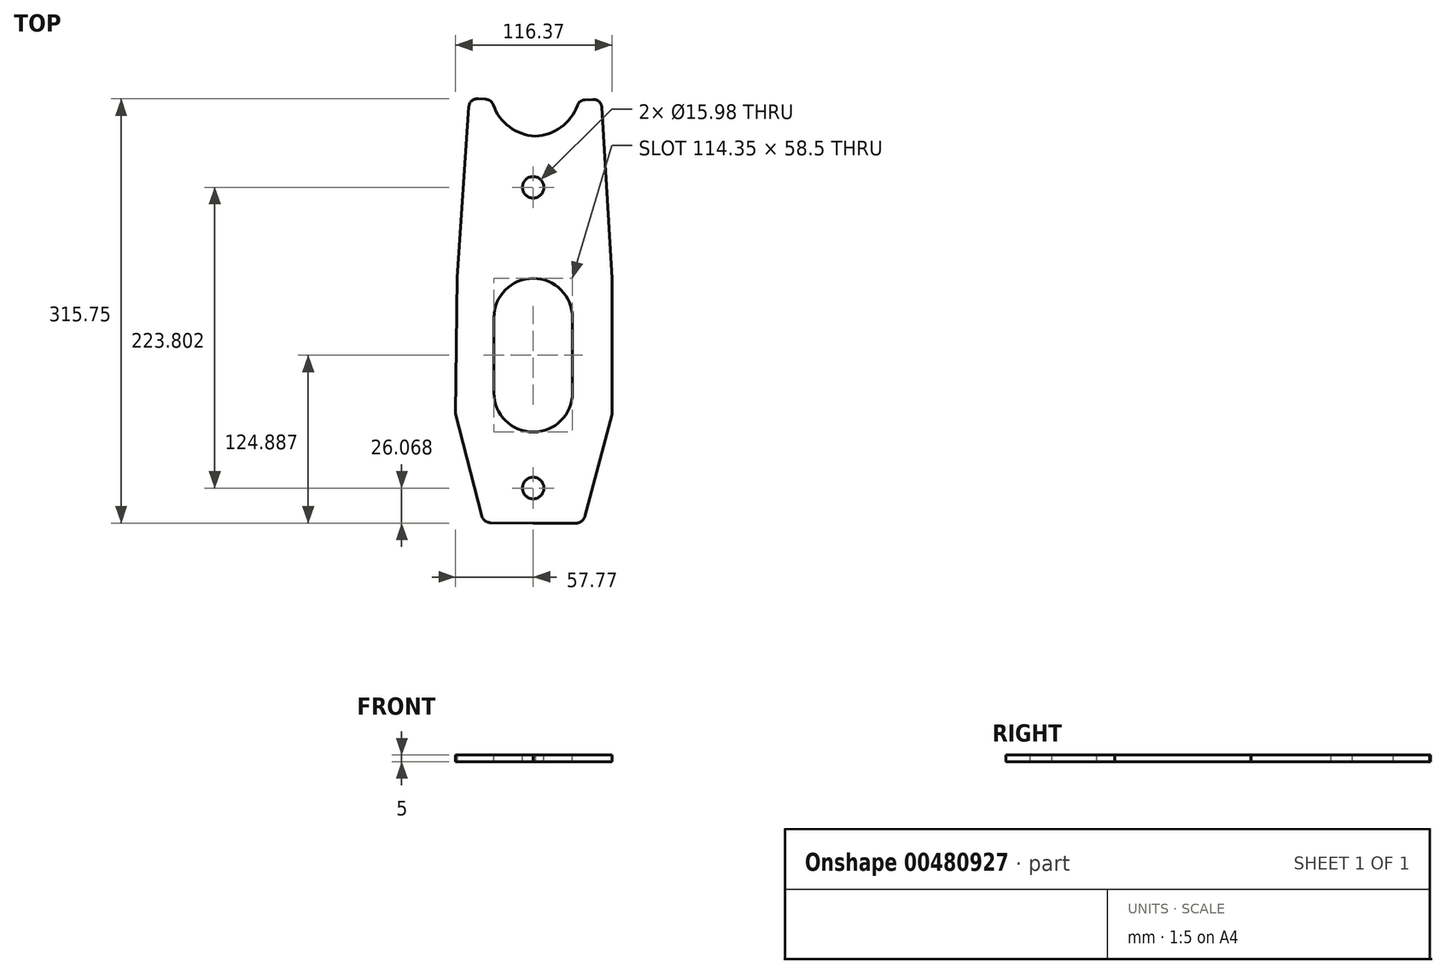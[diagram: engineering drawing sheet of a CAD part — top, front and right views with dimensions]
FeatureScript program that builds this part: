
annotation { "Feature Type Name" : "Feature", "Feature Type Description" : "" }
export const myFeature = defineFeature(function(context is Context, id is Id, definition is map)
    precondition{}
    {
        {
            var Q0;
            Q0=qCreatedBy(makeId("Top.planeOp"),FACE);
            var sketch = newSketch(context, id + "F0", { "sketchPlane" : qUnion([Q0])});
            skLineSegment(sketch, "E0", {"start": v(0, 0) * mm, "end": v(36.98, 0) * mm});
            skLineSegment(sketch, "E1", {"start": v(36.98, 0) * mm, "end": v(58.6, 0) * mm, "construction": true});
            skLineSegment(sketch, "E2", {"start": v(58.6, 0) * mm, "end": v(58.6, 80.74) * mm, "construction": true});
            skLineSegment(sketch, "E3", {"start": v(58.6, 80.74) * mm, "end": v(36.98, 0) * mm});
            skLineSegment(sketch, "E4", {"start": v(58.6, 80.74) * mm, "end": v(58.6, 182.06) * mm});
            skLineSegment(sketch, "E5", {"start": v(58.6, 182.06) * mm, "end": v(58.6, 315.68) * mm, "construction": true});
            skLineSegment(sketch, "E6", {"start": v(58.6, 315.68) * mm, "end": v(50.69, 315.68) * mm, "construction": true});
            skLineSegment(sketch, "E7", {"start": v(50.69, 315.68) * mm, "end": v(58.6, 182.06) * mm});
            skLineSegment(sketch, "E8", {"start": v(50.69, 315.68) * mm, "end": v(0, 312.67) * mm, "construction": true});
            skLineSegment(sketch, "E9", {"start": v(0, 312.67) * mm, "end": v(1.47, 287.85) * mm, "construction": true});
            skLineSegment(sketch, "E10", {"start": v(1.47, 287.85) * mm, "end": v(0, 322.82) * mm, "construction": true});
            skArc(sketch, "E11", {"start": v(1.47, 287.85) * mm, "mid": v(22.26, 295.8) * mm, "end": v(34.04, 314.7) * mm});
            skLineSegment(sketch, "E12", {"start": v(34.04, 314.7) * mm, "end": v(50.69, 315.68) * mm});
            skLineSegment(sketch, "E13", {"start": v(1.47, 287.85) * mm, "end": v(0, 0) * mm});
            skArc(sketch, "E14.MirrorCS", {"start": v(1.47, 287.85) * mm, "mid": v(-19.24, 296.02) * mm, "end": v(-30.83, 315.02) * mm});
            skLineSegment(sketch, "E15.MirrorCS", {"start": v(-47.46, 316.18) * mm, "end": v(3.2, 312.66) * mm, "construction": true});
            skLineSegment(sketch, "E16.MirrorCS", {"start": v(-47.46, 316.18) * mm, "end": v(-56.74, 182.65) * mm});
            skLineSegment(sketch, "E17.MirrorCS", {"start": v(-57.77, 81.33) * mm, "end": v(-56.74, 182.65) * mm});
            skLineSegment(sketch, "E18.MirrorCS", {"start": v(-57.77, 81.33) * mm, "end": v(-36.98, 0.38) * mm});
            skLineSegment(sketch, "E19.MirrorCS", {"start": v(0, 0) * mm, "end": v(-36.98, 0.38) * mm});
            skLineSegment(sketch, "E20", {"start": v(-47.46, 316.18) * mm, "end": v(-30.83, 315.02) * mm});
            skSolve(sketch);
        }
        {
            var Q0;
            Q0 = qSketchRegion(id + "F0", true);
            extrude(context, id + "F1", {"entities" : qUnion([Q0]), "depth" : 5 * mm});
        }
        {
            var Q0;
            Q0=makeQuery(id+"F1.opExtrude","CAP_FACE",FACE,{"disambiguationData":[OSD([sQuery(id+"F0.wireOp",EDGE,"E0"),sQuery(id+"F0.wireOp",EDGE,"E3"),sQuery(id+"F0.wireOp",EDGE,"E4"),sQuery(id+"F0.wireOp",EDGE,"E7"),sQuery(id+"F0.wireOp",EDGE,"E11"),sQuery(id+"F0.wireOp",EDGE,"E12"),sQuery(id+"F0.wireOp",EDGE,"E14.MirrorCS"),sQuery(id+"F0.wireOp",EDGE,"E16.MirrorCS"),sQuery(id+"F0.wireOp",EDGE,"E17.MirrorCS"),sQuery(id+"F0.wireOp",EDGE,"E18.MirrorCS"),sQuery(id+"F0.wireOp",EDGE,"E19.MirrorCS"),sQuery(id+"F0.wireOp",EDGE,"E20")])],"isStart":false});
            var sketch = newSketch(context, id + "F2", { "sketchPlane" : qUnion([Q0])});
            skLineSegment(sketch, "E21", {"start": v(0, 0) * mm, "end": v(0, 26.07) * mm, "construction": true});
            skLineSegment(sketch, "E22", {"start": v(0, 26.07) * mm, "end": v(0, 249.87) * mm, "construction": true});
            skCircle(sketch, "E23", {"center": v(0, 249.87) * mm, "radius": 7.99 * mm});
            skCircle(sketch, "E24", {"center": v(0, 26.07) * mm, "radius": 7.99 * mm});
            skSolve(sketch);
        }
        {
            var Q0;
            Q0 = qSketchRegion(id + "F2", true);
            extrude(context, id + "F3", {"entities" : qUnion([Q0]), "operationType" : NewBodyOperationType.REMOVE, "oppositeDirection" : true, "depth" : 25.4 * mm});
        }
        {
            var Q0;
            Q0=makeQuery(id+"F1.opExtrude","CAP_FACE",FACE,{"disambiguationData":[OSD([sQuery(id+"F0.wireOp",EDGE,"E0"),sQuery(id+"F0.wireOp",EDGE,"E3"),sQuery(id+"F0.wireOp",EDGE,"E4"),sQuery(id+"F0.wireOp",EDGE,"E7"),sQuery(id+"F0.wireOp",EDGE,"E11"),sQuery(id+"F0.wireOp",EDGE,"E12"),sQuery(id+"F0.wireOp",EDGE,"E14.MirrorCS"),sQuery(id+"F0.wireOp",EDGE,"E16.MirrorCS"),sQuery(id+"F0.wireOp",EDGE,"E17.MirrorCS"),sQuery(id+"F0.wireOp",EDGE,"E18.MirrorCS"),sQuery(id+"F0.wireOp",EDGE,"E19.MirrorCS"),sQuery(id+"F0.wireOp",EDGE,"E20")])],"isStart":false});
            var sketch = newSketch(context, id + "F4", { "sketchPlane" : qUnion([Q0])});
            skSolve(sketch);
        }
        {
            var Q0;
            Q0=makeQuery(id+"F4.imprint","IMPRINT",FACE,{"disambiguationData":[TD([[makeQuery(id+"F4.imprint","IMPRINT",EDGE,{"derivedFrom":makeQuery(id+"F1.opExtrude","CAP_EDGE",EDGE,{"disambiguationData":[OSD([sQuery(id+"F0.wireOp",EDGE,"E0")])],"isStart":false})}),1.0]])]});
            var sketch = newSketch(context, id + "F5", { "sketchPlane" : qUnion([Q0])});
            skLineSegment(sketch, "E25", {"start": v(0, 0) * mm, "end": v(0, 182.06) * mm, "construction": true});
            skLineSegment(sketch, "E26", {"start": v(0, 182.06) * mm, "end": v(0, 67.71) * mm, "construction": true});
            skLineSegment(sketch, "E27", {"start": v(0, 67.71) * mm, "end": v(0, 96.96) * mm, "construction": true});
            skLineSegment(sketch, "E28", {"start": v(0, 96.96) * mm, "end": v(29.25, 96.96) * mm, "construction": true});
            skArc(sketch, "E29", {"start": v(0, 67.71) * mm, "mid": v(20.68, 76.28) * mm, "end": v(29.25, 96.96) * mm});
            skArc(sketch, "E30", {"start": v(0, 67.71) * mm, "mid": v(-20.68, 76.28) * mm, "end": v(-29.25, 96.96) * mm});
            skLineSegment(sketch, "E31", {"start": v(0, 182.06) * mm, "end": v(0, 152.81) * mm, "construction": true});
            skArc(sketch, "E32", {"start": v(0, 182.06) * mm, "mid": v(20.68, 173.5) * mm, "end": v(29.25, 152.81) * mm});
            skArc(sketch, "E33", {"start": v(0, 182.06) * mm, "mid": v(-20.68, 173.5) * mm, "end": v(-29.25, 152.81) * mm});
            skLineSegment(sketch, "E34", {"start": v(-29.25, 152.81) * mm, "end": v(-29.25, 96.96) * mm});
            skLineSegment(sketch, "E35", {"start": v(29.25, 152.81) * mm, "end": v(29.25, 96.96) * mm});
            skSolve(sketch);
        }
        {
            var Q0;
            Q0 = qSketchRegion(id + "F5", true);
            extrude(context, id + "F6", {"entities" : qUnion([Q0]), "operationType" : NewBodyOperationType.REMOVE, "oppositeDirection" : true, "depth" : 25.4 * mm});
        }
        {
            var Q0;
            Q0=makeQuery(id+"F1.opExtrude","SWEPT_EDGE",EDGE,{"disambiguationData":[OSD([sQuery(id+"F0.wireOp",EDGE,"E18.MirrorCS"),sQuery(id+"F0.wireOp",EDGE,"E19.MirrorCS")])]});
            var Q1;
            Q1=makeQuery(id+"F1.opExtrude","SWEPT_EDGE",EDGE,{"disambiguationData":[OSD([sQuery(id+"F0.wireOp",EDGE,"E0"),sQuery(id+"F0.wireOp",EDGE,"E3")])]});
            var Q2;
            Q2=makeQuery(id+"F1.opExtrude","SWEPT_EDGE",EDGE,{"disambiguationData":[OSD([sQuery(id+"F0.wireOp",EDGE,"E7"),sQuery(id+"F0.wireOp",EDGE,"E12")])]});
            var Q3;
            Q3=makeQuery(id+"F1.opExtrude","SWEPT_EDGE",EDGE,{"disambiguationData":[OSD([sQuery(id+"F0.wireOp",EDGE,"E11"),sQuery(id+"F0.wireOp",EDGE,"E12")])]});
            var Q4;
            Q4=makeQuery(id+"F1.opExtrude","SWEPT_EDGE",EDGE,{"disambiguationData":[OSD([sQuery(id+"F0.wireOp",EDGE,"E14.MirrorCS"),sQuery(id+"F0.wireOp",EDGE,"E20")])]});
            var Q5;
            Q5=makeQuery(id+"F1.opExtrude","SWEPT_EDGE",EDGE,{"disambiguationData":[OSD([sQuery(id+"F0.wireOp",EDGE,"E16.MirrorCS"),sQuery(id+"F0.wireOp",EDGE,"E20")])]});
            fillet(context, id + "F7", {"entities" : qUnion([Q0, Q1, Q2, Q3, Q4, Q5]), "radius" : 6.35 * mm, "tangentPropagation" : true, "allowEdgeOverflow" : false});
        }
    });
